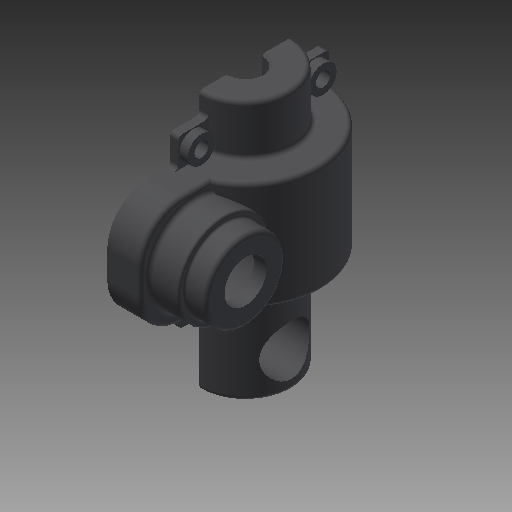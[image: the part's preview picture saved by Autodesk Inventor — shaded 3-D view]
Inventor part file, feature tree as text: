
AUTODESK INVENTOR PART (.ipt)
format: ipt  version: 2019 (Build 230136000, 136)  size: 477,696 bytes
history: native  units: mm
features: extrude x10, fillet x6, sketch x5, projected_geometry x2, plane x1, revolve x1, split x1, hole x1, chamfer x1, mirror x1
ambient origin geometry x8: Origin, YZ Plane, XZ Plane, XY Plane, X Axis, Y Axis, Z Axis, Center Point
bodies: Solid1 (feature_tree)
feature tree (29):
  extrude  "Extrusion1"  Depth=62.0mm TaperAngle=0.0deg
  plane  "Work Plane1"
  extrude  "Extrusion2"  Depth=36.0mm
  sketch  "Sketch3"  dims[d5=26.0mm d6=0.0mm d7=22.0mm]
  extrude  "Extrusion3"  Depth=22.0mm
  extrude  "Extrusion4"  Depth=15.0mm
  extrude  "Extrusion5"  Depth=16.0mm TaperAngle=0.0deg
  extrude  "Extrusion6"  Depth=1.0mm TaperAngle=0.0deg
  revolve  "Revolution1"  [1 undecoded]
  split  "Split1"
  extrude  "Extrusion7"  Depth=1.0mm
  extrude  "Extrusion8"  Depth=1.0mm TaperAngle=0.0deg
  fillet  "Fillet7"  Radius=34.0mm
  fillet  "Fillet8"  Radius=9.05mm
  fillet  "Fillet9"  Radius=9.0mm
  sketch  "Sketch5"  dims[d10=13.0mm d11=16.0mm d12=0.0mm d13=30.0mm d14=0.0mm d15=19.0mm d16=17.0mm d17=40.0mm d18=0.0mm d19=34.0mm d20=0.0mm d25=9.05mm d26=9.0mm d28=6.0mm d29=4.05mm d30=2.0mm d31=14.65mm d32=90.0deg d34=12.0mm d35=8.374731mm d36=56.0mm d37=0.0mm d40=10.0mm d41=56.0mm d42=0.0mm d47=10.0mm d48=1.0mm d49=0.5mm d51=7.0mm d52=7.0mm d53=3.5mm d54=3.5mm d56=2.0mm d57=0.0mm d67=26.0mm d78=6.5mm d79=6.5mm d80=6.5mm d81=6.5mm d82=4.0mm d83=0.0mm d84=3.4mm d85=6.0mm d86=6.3mm d87=2.0mm d88=90.0deg d89=4.0mm d90=20.594885mm d91=2.0mm d92=0.5mm d93=2.0mm d94=45.0deg d95=1.0mm d96=1.0mm d97=1.0mm d99=0.625269mm]
  extrude  "Extrusion9"  Depth=1.0mm
  extrude  "Extrusion11"  Depth=1.0mm
  hole  "Hole2"  [1 undecoded]
  chamfer  "Chamfer1"  Distance=14.65mm
  fillet  "Fillet13"  [1 undecoded]
  fillet  "Fillet14"  Radius=12.0mm
  fillet  "Fillet15"  Radius=8.374731mm
  mirror  "Mirror1"
  sketch  "Sketch1"  dims[d0=22.0mm d1=62.0mm d2=0.0mm]
  sketch  "Sketch2"  dims[d3=-24.0mm d4=36.0mm]
  sketch  "Sketch4"  dims[d8=20.0mm d9=15.0mm]
  projected_geometry  "Project Cut Edges1"
  projected_geometry  "Project Cut Edges2"
note: 3 required parameter values undecoded (feature->parameter linkage not recoverable at this tier; creation-order binding heuristic only, values carry confidence <= 0.55)